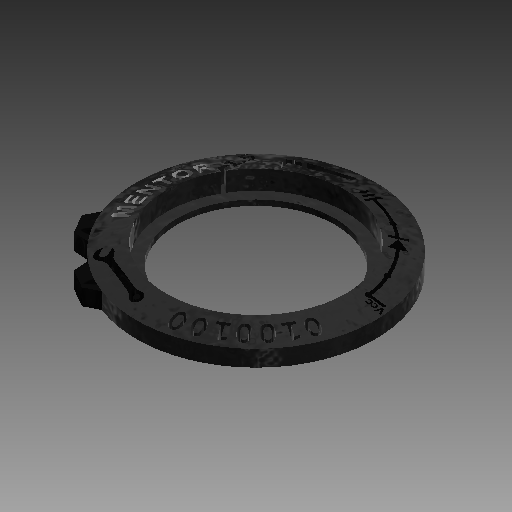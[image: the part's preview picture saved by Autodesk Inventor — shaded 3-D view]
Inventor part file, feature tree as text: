
AUTODESK INVENTOR PART (.ipt)
format: ipt  version: 2017 (Build 210142000, 142)  size: 1,403,904 bytes
history: native  units: mm (DEFAULTED — no unit token found)
features: other x5, extrude x1, projected_geometry x1
ambient origin geometry x8: Origin, YZ Plane, XZ Plane, XY Plane, X Axis, Y Axis, Z Axis, Center Point
bodies: Solid1 (feature_tree)
feature tree (7):
  other  "Mentor Ring.iam"
  other  "Mentor-Code ring.ipt:1"
  other  "Mentor-Mechanical ring.ipt:1"
  other  "Mentor-Electrical ring.ipt:1"
  other  "Mentor-CAD ring.ipt:1"
  extrude  "Extrusion1"  Depth=10.0mm
  projected_geometry  "Projected Loop1"
